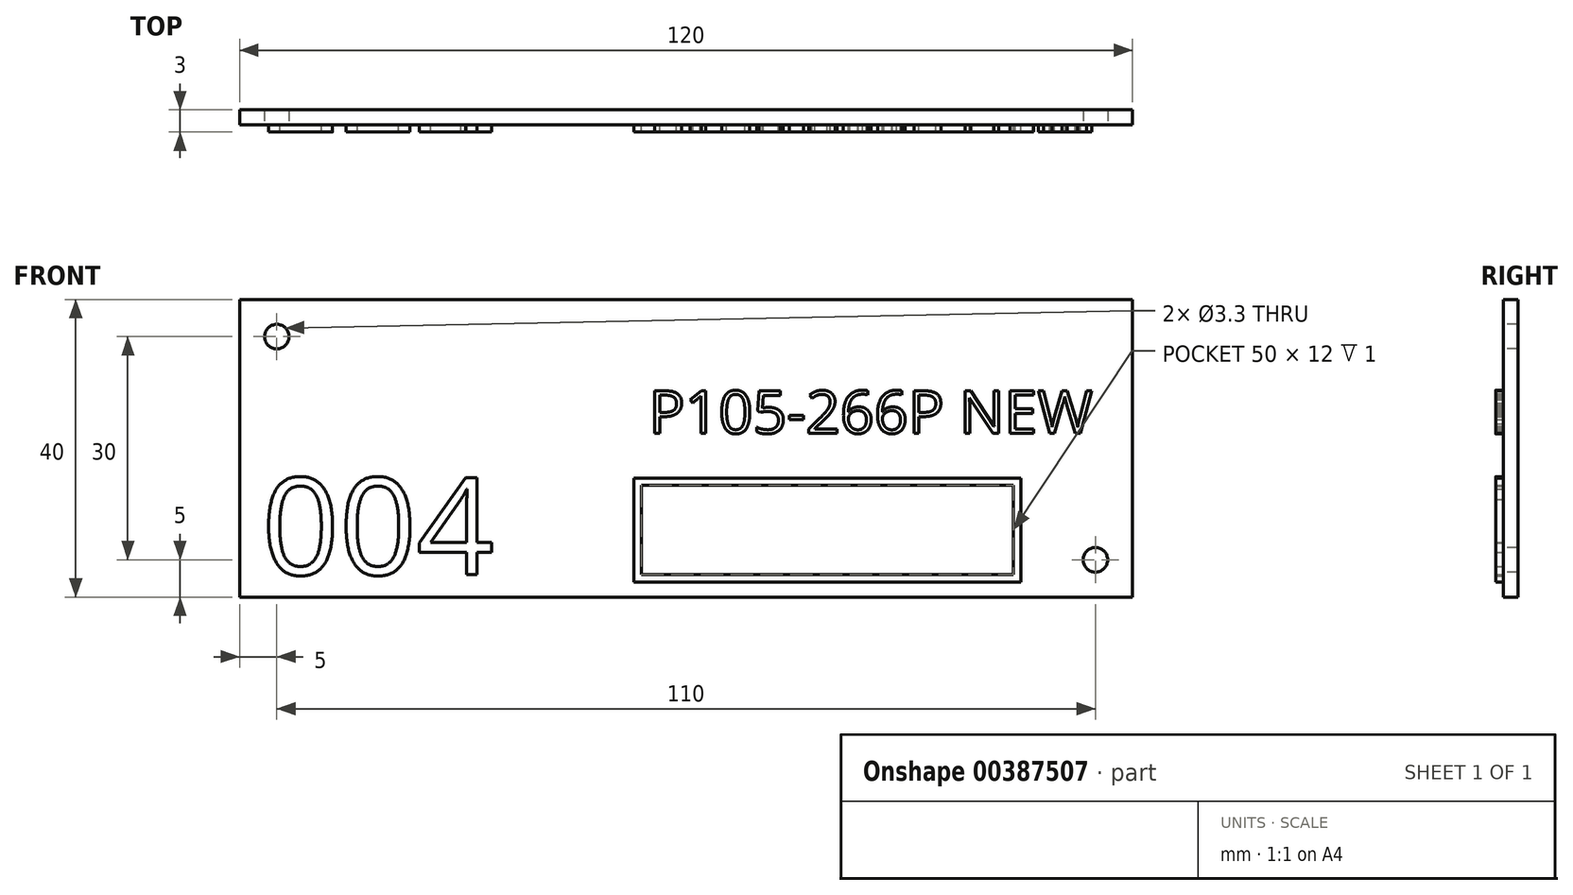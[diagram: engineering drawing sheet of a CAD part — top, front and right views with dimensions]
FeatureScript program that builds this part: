
annotation { "Feature Type Name" : "Feature", "Feature Type Description" : "" }
export const myFeature = defineFeature(function(context is Context, id is Id, definition is map)
    precondition{}
    {
        {
            var Q0;
            Q0=qCreatedBy(makeId("Front.planeOp"),FACE);
            var sketch = newSketch(context, id + "F0", { "sketchPlane" : qUnion([Q0])});
            skLineSegment(sketch, "E0.bottom", {"start": v(60, -20) * mm, "end": v(-60, -20) * mm});
            skLineSegment(sketch, "E0.top", {"start": v(60, 20) * mm, "end": v(-60, 20) * mm});
            skLineSegment(sketch, "E0.left", {"start": v(60, -20) * mm, "end": v(60, 20) * mm});
            skLineSegment(sketch, "E0.right", {"start": v(-60, -20) * mm, "end": v(-60, 20) * mm});
            skPoint(sketch, "E0.middle", {"position": v(0, 0) * mm});
            skSolve(sketch);
        }
        {
            var Q0;
            Q0=makeQuery(id+"F0.imprint","IMPRINT",FACE,{"disambiguationData":[TD([[makeQuery(id+"F0.imprint","IMPRINT",EDGE,{"derivedFrom":sQuery(id+"F0.wireOp",EDGE,"E0.bottom")}),-1.0]])]});
            extrude(context, id + "F1", {"entities" : qUnion([Q0]), "depth" : 2 * mm});
        }
        {
            var Q0;
            Q0=makeQuery(id+"F1.opExtrude","CAP_FACE",FACE,{"disambiguationData":[OSD([sQuery(id+"F0.wireOp",EDGE,"E0.bottom"),sQuery(id+"F0.wireOp",EDGE,"E0.top"),sQuery(id+"F0.wireOp",EDGE,"E0.left"),sQuery(id+"F0.wireOp",EDGE,"E0.right")])],"isStart":false});
            var sketch = newSketch(context, id + "F2", { "sketchPlane" : qUnion([Q0])});
            skPoint(sketch, "E1", {"position": v(-55, 15) * mm});
            skPoint(sketch, "E2", {"position": v(55, -15) * mm});
            skSolve(sketch);
        }
        {
            var Q0;
            Q0=sQuery(id+"F2.wireOp",VERTEX,"E1");
            var Q1;
            Q1=sQuery(id+"F2.wireOp",VERTEX,"E2");
            var Q2;
            Q2=makeQuery(id+"F1.opExtrude","SWEPT_BODY",BODY,{"disambiguationData":[OSD([sQuery(id+"F0.wireOp",EDGE,"E0.bottom"),sQuery(id+"F0.wireOp",EDGE,"E0.top"),sQuery(id+"F0.wireOp",EDGE,"E0.left"),sQuery(id+"F0.wireOp",EDGE,"E0.right")])]});
            hole(context, id + "F3", {"style" : HoleStyle.SIMPLE, "endStyle" : HoleEndStyle.THROUGH, "holeDiameter" : 3.3 * mm, "locations" : qUnion([Q0, Q1]), "scope" : qUnion([Q2]), "isTappedThrough" : true});
        }
        {
            var Q0;
            Q0=makeQuery(id+"F1.opExtrude","CAP_FACE",FACE,{"disambiguationData":[OSD([sQuery(id+"F0.wireOp",EDGE,"E0.bottom"),sQuery(id+"F0.wireOp",EDGE,"E0.top"),sQuery(id+"F0.wireOp",EDGE,"E0.left"),sQuery(id+"F0.wireOp",EDGE,"E0.right")])],"isStart":false});
            var sketch = newSketch(context, id + "F4", { "sketchPlane" : qUnion([Q0])});
            skText(sketch, "E3", { "text": "P105-266P NEW", "fontName": "OpenSans-Regular.ttf"});
            const initialGuessF4  = {"E3": [-0.005, 0.002, 1, 0, 0.00576]};
            skSetInitialGuess(sketch, initialGuessF4);
            skSolve(sketch);
        }
        {
            var Q0;
            Q0=qSketchRegion(id+"F4",true);
            extrude(context, id + "F5", {"entities" : qUnion([Q0]), "operationType" : NewBodyOperationType.ADD, "depth" : 1 * mm});
        }
        {
            var Q0;
            {var subQ0=sQuery(id+"F0.wireOp",EDGE,"E0.top");var subQ1=sQuery(id+"F0.wireOp",EDGE,"E0.left");var subQ2=sQuery(id+"F0.wireOp",EDGE,"E0.right");var subQ3=sQuery(id+"F0.wireOp",EDGE,"E0.bottom");Q0=makeQuery(id+"F5.boolean.opBoolean","SPLIT",FACE,{"disambiguationData":[TD([makeQuery(id+"F1.opExtrude","SWEPT_FACE",FACE,{"disambiguationData":[OSD([subQ3])]})])],"derivedFrom":makeQuery(id+"F1.opExtrude","CAP_FACE",FACE,{"disambiguationData":[OSD([subQ3,subQ0,subQ1,subQ2])],"isStart":false})});}
            var sketch = newSketch(context, id + "F6", { "sketchPlane" : qUnion([Q0])});
            skText(sketch, "E4", { "text": "004", "fontName": "OpenSans-Regular.ttf"});
            const initialGuessF6  = {"E4": [-0.057, -0.017, 1, 0, 0.0131]};
            skSetInitialGuess(sketch, initialGuessF6);
            skSolve(sketch);
        }
        {
            var Q0;
            Q0=qSketchRegion(id+"F6",true);
            extrude(context, id + "F7", {"entities" : qUnion([Q0]), "operationType" : NewBodyOperationType.ADD, "depth" : 1 * mm});
        }
        {
            var Q0;
            {var subQ46=sQuery(id+"F0.wireOp",EDGE,"E0.top");var subQ48=sQuery(id+"F0.wireOp",EDGE,"E0.left");var subQ66=sQuery(id+"F0.wireOp",EDGE,"E0.right");var subQ76=sQuery(id+"F0.wireOp",EDGE,"E0.bottom");var subQ77=makeQuery(id+"F1.opExtrude","SWEPT_FACE",FACE,{"disambiguationData":[OSD([subQ76])]});Q0=makeQuery(id+"F7.boolean.opBoolean","SPLIT",FACE,{"disambiguationData":[TD([subQ77])],"derivedFrom":makeQuery(id+"F5.boolean.opBoolean","SPLIT",FACE,{"disambiguationData":[TD([subQ77])],"derivedFrom":makeQuery(id+"F1.opExtrude","CAP_FACE",FACE,{"disambiguationData":[OSD([subQ76,subQ46,subQ48,subQ66])],"isStart":false})})});}
            var sketch = newSketch(context, id + "F8", { "sketchPlane" : qUnion([Q0])});
            skLineSegment(sketch, "E5.bottom", {"start": v(45, -18) * mm, "end": v(-7, -18) * mm});
            skLineSegment(sketch, "E5.top", {"start": v(45, -4) * mm, "end": v(-7, -4) * mm});
            skLineSegment(sketch, "E5.left", {"start": v(45, -18) * mm, "end": v(45, -4) * mm});
            skLineSegment(sketch, "E5.right", {"start": v(-7, -18) * mm, "end": v(-7, -4) * mm});
            skPoint(sketch, "E5.middle", {"position": v(19, -11) * mm});
            skLineSegment(sketch, "E6.0", {"start": v(44, -5) * mm, "end": v(-6, -5) * mm});
            skLineSegment(sketch, "E6.1", {"start": v(44, -17) * mm, "end": v(44, -5) * mm});
            skLineSegment(sketch, "E6.2", {"start": v(44, -17) * mm, "end": v(-6, -17) * mm});
            skLineSegment(sketch, "E6.3", {"start": v(-6, -17) * mm, "end": v(-6, -5) * mm});
            skSolve(sketch);
        }
        {
            var Q0;
            Q0=makeQuery(id+"F8.imprint","IMPRINT",FACE,{"disambiguationData":[TD([[makeQuery(id+"F8.imprint","IMPRINT",EDGE,{"derivedFrom":sQuery(id+"F8.wireOp",EDGE,"E5.bottom")}),-1.0]])]});
            extrude(context, id + "F9", {"entities" : qUnion([Q0]), "operationType" : NewBodyOperationType.ADD, "depth" : 1 * mm});
        }
    });
